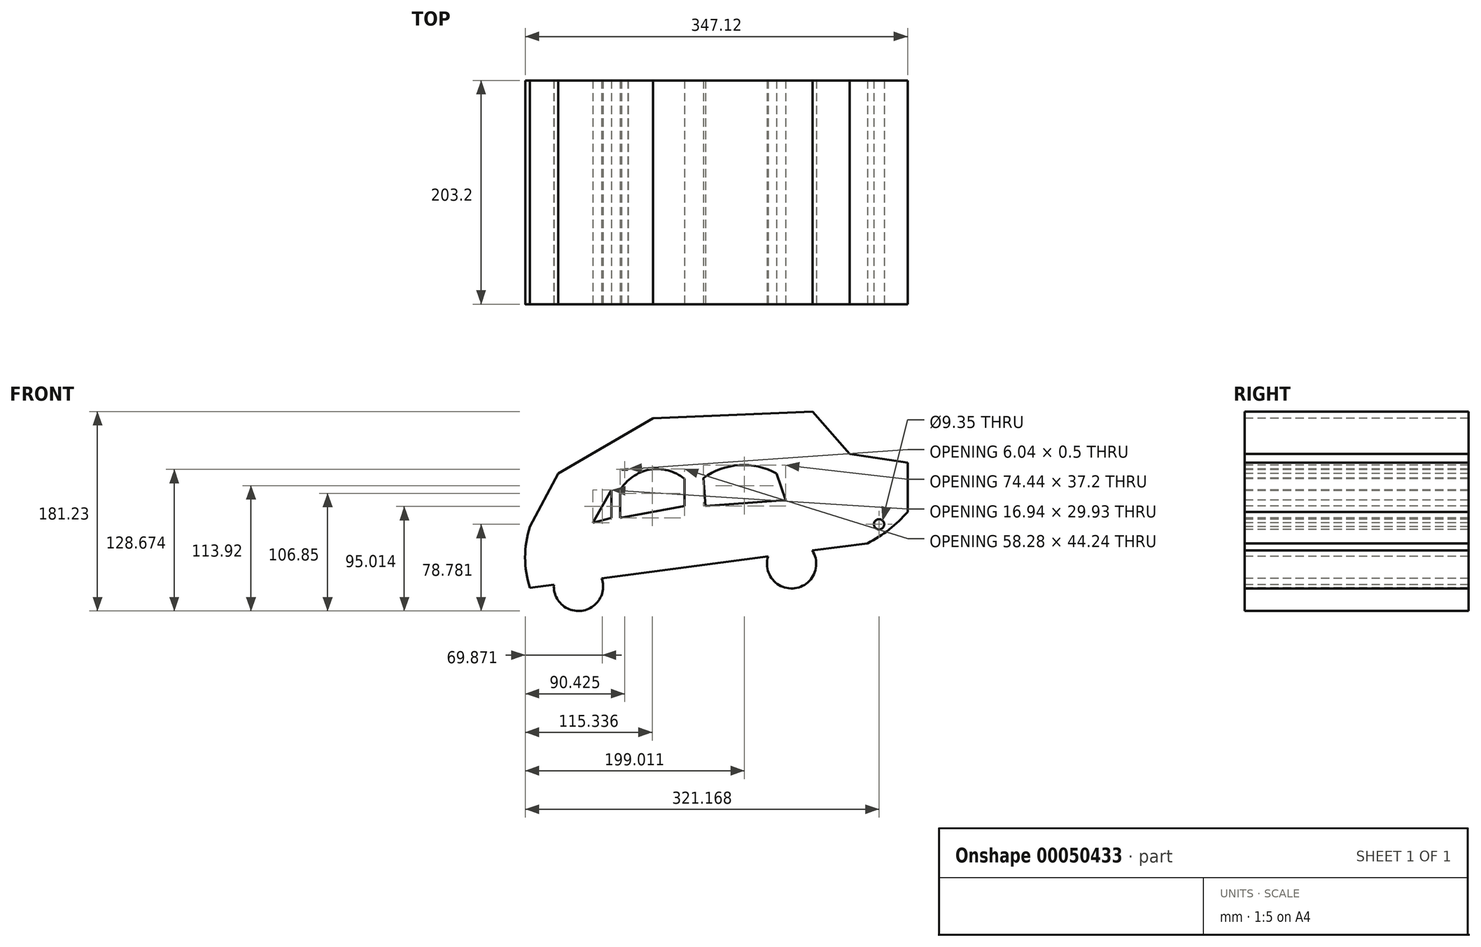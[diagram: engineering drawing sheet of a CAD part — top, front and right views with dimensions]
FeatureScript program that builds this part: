
annotation { "Feature Type Name" : "Feature", "Feature Type Description" : "" }
export const myFeature = defineFeature(function(context is Context, id is Id, definition is map)
    precondition{}
    {
        {
            var Q0;
            Q0=qCreatedBy(makeId("Front.planeOp"),FACE);
            var sketch = newSketch(context, id + "F0", { "sketchPlane" : qUnion([Q0])});
            skLineSegment(sketch, "E0", {"start": v(-87.95, 38.3) * mm, "end": v(-82.08, 38.3) * mm});
            skPoint(sketch, "E1.end.orphan", {"position": v(-89.54, 29.08) * mm});
            skPoint(sketch, "E2.orphan", {"position": v(-97, 19.86) * mm});
            skPoint(sketch, "E3.start.orphan", {"position": v(-82.08, 38.3) * mm});
            skPoint(sketch, "E4.end.orphan", {"position": v(-104.37, 19.86) * mm});
            skLineSegment(sketch, "E5", {"start": v(83.15, 6.68) * mm, "end": v(135.38, -4.36) * mm});
            skLineSegment(sketch, "E6", {"start": v(-87.95, 38.3) * mm, "end": v(56.5, 50.16) * mm});
            skLineSegment(sketch, "E7", {"start": v(56.5, 50.16) * mm, "end": v(83.15, 6.68) * mm});
            skLineSegment(sketch, "E8", {"start": v(135.38, -4.36) * mm, "end": v(135.38, -28.6) * mm});
            skLineSegment(sketch, "E9", {"start": v(135.38, -28.6) * mm, "end": v(-171.1, -68.98) * mm});
            skLineSegment(sketch, "E10", {"start": v(-82.08, 38.3) * mm, "end": v(-81.9, 38.8) * mm});
            skLineSegment(sketch, "E11", {"start": v(-87.95, 38.3) * mm, "end": v(-59.4, 85.03) * mm});
            skLineSegment(sketch, "E12", {"start": v(-59.4, 85.03) * mm, "end": v(85.4, 91.1) * mm});
            skArc(sketch, "E13", {"start": v(56.5, 50.16) * mm, "mid": v(73, 69.2) * mm, "end": v(85.4, 91.1) * mm});
            skLineSegment(sketch, "E14", {"start": v(85.4, 91.1) * mm, "end": v(119, 52.74) * mm});
            skArc(sketch, "E15", {"start": v(83.15, 6.68) * mm, "mid": v(103.75, 27.62) * mm, "end": v(119, 52.74) * mm});
            skLineSegment(sketch, "E16", {"start": v(119, 52.74) * mm, "end": v(171.77, 44.67) * mm});
            skLineSegment(sketch, "E17", {"start": v(171.77, 44.67) * mm, "end": v(171.77, 0) * mm});
            skArc(sketch, "E18", {"start": v(135.38, -4.36) * mm, "mid": v(156.74, 17.8) * mm, "end": v(171.77, 44.67) * mm});
            skArc(sketch, "E19", {"start": v(135.38, -28.6) * mm, "mid": v(154.96, -16.06) * mm, "end": v(171.77, 0) * mm});
            skLineSegment(sketch, "E20", {"start": v(-17.86, -48.78) * mm, "end": v(-21.73, 43.74) * mm});
            skLineSegment(sketch, "E21", {"start": v(-89.15, 19.35) * mm, "end": v(-89.15, -5.4) * mm});
            skLineSegment(sketch, "E22", {"start": v(-89.15, -5.4) * mm, "end": v(-30.88, 5.23) * mm});
            skLineSegment(sketch, "E23", {"start": v(-30.88, 5.23) * mm, "end": v(-30.88, 29.97) * mm});
            skArc(sketch, "E24", {"start": v(-30.88, 29.97) * mm, "mid": v(-62.5, 38.25) * mm, "end": v(-89.15, 19.35) * mm});
            skLineSegment(sketch, "E25", {"start": v(-11.66, 5.2) * mm, "end": v(60.88, 10.64) * mm});
            skLineSegment(sketch, "E26", {"start": v(60.88, 10.64) * mm, "end": v(52.83, 34.77) * mm});
            skLineSegment(sketch, "E27", {"start": v(-11.66, 5.2) * mm, "end": v(-13.56, 30.57) * mm});
            skArc(sketch, "E28", {"start": v(52.83, 34.77) * mm, "mid": v(19.02, 42.4) * mm, "end": v(-13.56, 30.57) * mm});
            skCircle(sketch, "E29", {"center": v(-126.97, -67.77) * mm, "radius": 22.35 * mm});
            skCircle(sketch, "E30", {"center": v(66.46, -47.27) * mm, "radius": 22.35 * mm});
            skCircle(sketch, "E31", {"center": v(145.82, -11.34) * mm, "radius": 4.67 * mm});
            skCircle(sketch, "E32", {"center": v(167.1, 8.24) * mm, "radius": 4.67 * mm});
            skArc(sketch, "E33", {"start": v(-171.1, -13.62) * mm, "mid": v(-175.35, -41.3) * mm, "end": v(-171.1, -68.98) * mm});
            skPoint(sketch, "E34.orphan", {"position": v(-122.06, 0) * mm});
            skLineSegment(sketch, "E35", {"start": v(-97, 19.86) * mm, "end": v(-97, -5.4) * mm});
            skLineSegment(sketch, "E36", {"start": v(-97, -5.4) * mm, "end": v(-113.95, -10.07) * mm});
            skPoint(sketch, "E37.start.orphan", {"position": v(-110.85, 0) * mm});
            skLineSegment(sketch, "E38", {"start": v(-97, 19.86) * mm, "end": v(-113.95, -10.07) * mm});
            skLineSegment(sketch, "E39", {"start": v(-125.85, -8.3) * mm, "end": v(-95.78, -59.05) * mm});
            skLineSegment(sketch, "E40", {"start": v(83.15, 6.68) * mm, "end": v(34.57, -41.88) * mm});
            skPoint(sketch, "E41.end.orphan", {"position": v(-165.23, -13.62) * mm});
            skLineSegment(sketch, "E42", {"start": v(-171.1, -13.62) * mm, "end": v(-125.85, -8.3) * mm});
            skLineSegment(sketch, "E43", {"start": v(-171.1, -13.62) * mm, "end": v(-87.95, 38.3) * mm});
            skLineSegment(sketch, "E44", {"start": v(-171.1, -13.62) * mm, "end": v(-86.57, 39.16) * mm});
            skLineSegment(sketch, "E45", {"start": v(-87.95, 38.3) * mm, "end": v(-86.57, 39.16) * mm});
            skLineSegment(sketch, "E46", {"start": v(-59.4, 85.03) * mm, "end": v(-145.43, 34.76) * mm});
            skLineSegment(sketch, "E47", {"start": v(-145.43, 34.76) * mm, "end": v(-171.1, -13.62) * mm});
            skSolve(sketch);
        }
        {
            var Q0;
            Q0 = qSketchRegion(id + "F0", true);
            extrude(context, id + "F1", {"entities" : qUnion([Q0]), "oppositeDirection" : true, "depth" : 76.2 * mm});
        }
        {
            var Q0;
            Q0 = qSketchRegion(id + "F0", true);
            extrude(context, id + "F2", {"entities" : qUnion([Q0]), "operationType" : NewBodyOperationType.ADD, "depth" : 127 * mm});
        }
    });
